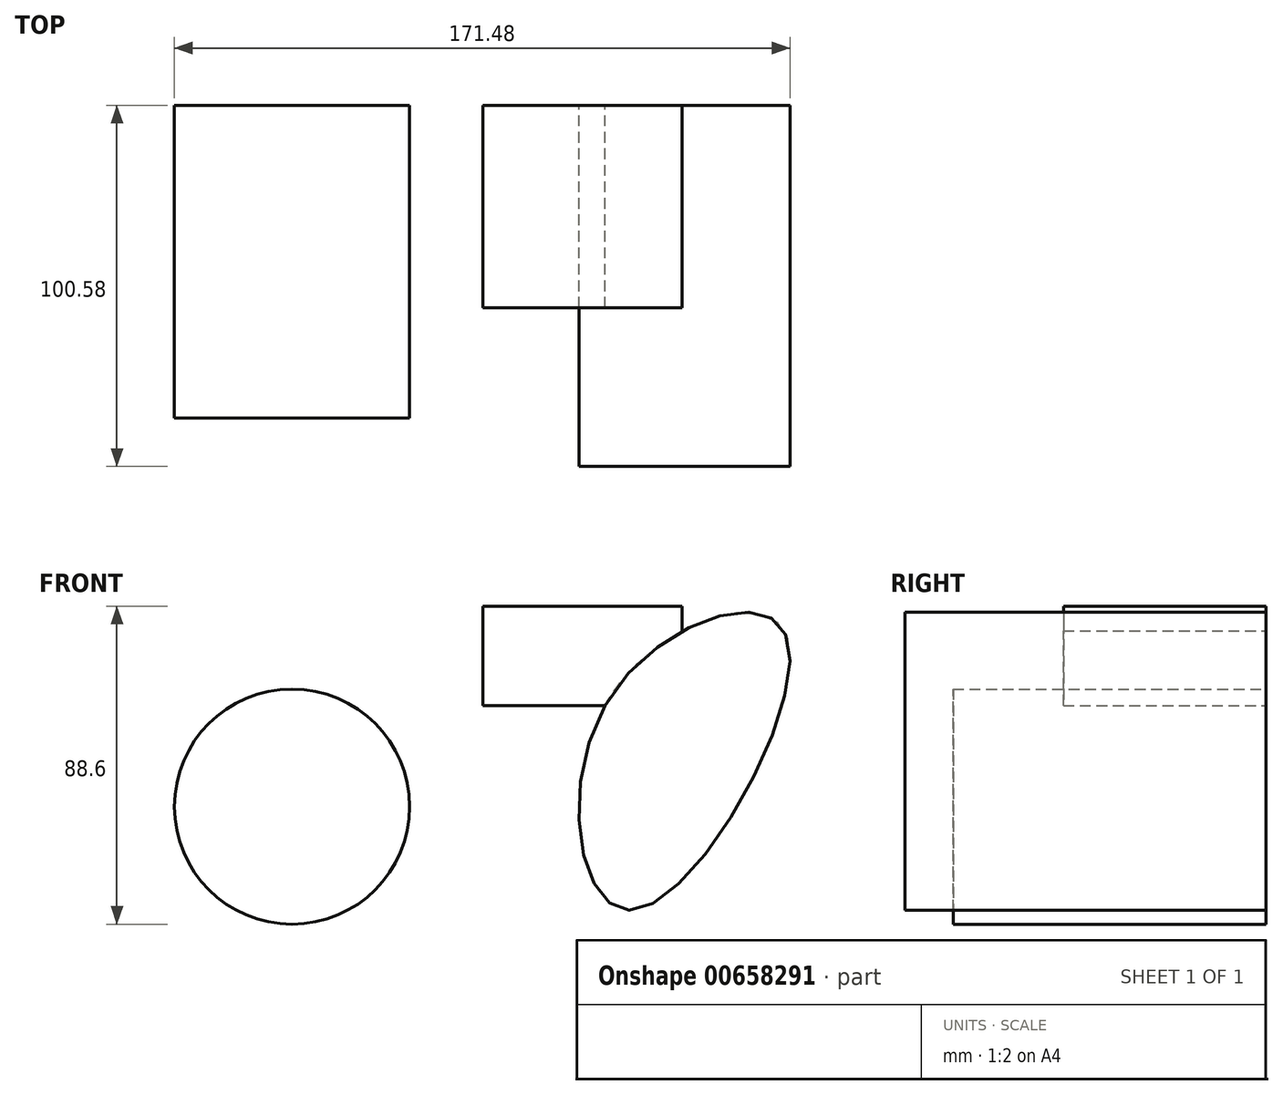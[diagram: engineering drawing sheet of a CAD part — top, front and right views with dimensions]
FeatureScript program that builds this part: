
annotation { "Feature Type Name" : "Feature", "Feature Type Description" : "" }
export const myFeature = defineFeature(function(context is Context, id is Id, definition is map)
    precondition{}
    {
        {
            var Q0;
            Q0=qCreatedBy(makeId("Front.planeOp"),FACE);
            var sketch = newSketch(context, id + "F0", { "sketchPlane" : qUnion([Q0])});
            skLineSegment(sketch, "E0.bottom", {"start": v(-113.94, 27.68) * mm, "end": v(-58.47, 27.68) * mm});
            skLineSegment(sketch, "E0.top", {"start": v(-113.94, 0) * mm, "end": v(-58.47, 0) * mm});
            skLineSegment(sketch, "E0.left", {"start": v(-113.94, 27.68) * mm, "end": v(-113.94, 0) * mm});
            skLineSegment(sketch, "E0.right", {"start": v(-58.47, 27.68) * mm, "end": v(-58.47, 0) * mm});
            skSolve(sketch);
        }
        {
            var Q0;
            Q0=makeQuery(id+"F0.imprint","IMPRINT",FACE,{"disambiguationData":[TD([[makeQuery(id+"F0.imprint","IMPRINT",EDGE,{"derivedFrom":sQuery(id+"F0.wireOp",EDGE,"E0.bottom")}),-1.0]])]});
            extrude(context, id + "F1", {"entities" : qUnion([Q0]), "depth" : 56.4 * mm, "offsetDistance" : 25.4 * mm});
        }
        {
            var Q0;
            Q0=qCreatedBy(makeId("Front.planeOp"),FACE);
            var sketch = newSketch(context, id + "F2", { "sketchPlane" : qUnion([Q0])});
            skFitSpline(sketch, "E1", {"points": [v(-79.93, 0) * mm, v(-29.7, 20.08) * mm, v(-72.08, -57.04) * mm, v(-79.93, 0) * mm]});
            skSolve(sketch);
        }
        {
            var Q0;
            Q0=makeQuery(id+"F2.imprint","IMPRINT",FACE,{"disambiguationData":[TD([[makeQuery(id+"F2.imprint","IMPRINT",EDGE,{"derivedFrom":sQuery(id+"F2.wireOp",EDGE,"E1")}),-1.0]])]});
            extrude(context, id + "F3", {"entities" : qUnion([Q0]), "operationType" : NewBodyOperationType.ADD, "depth" : 100.58 * mm, "offsetDistance" : 25.4 * mm});
        }
        {
            var Q0;
            Q0=qCreatedBy(makeId("Front.planeOp"),FACE);
            var sketch = newSketch(context, id + "F4", { "sketchPlane" : qUnion([Q0])});
            skCircle(sketch, "E2", {"center": v(-167.1, -28.16) * mm, "radius": 32.77 * mm});
            skSolve(sketch);
        }
        {
            var Q0;
            Q0=makeQuery(id+"F4.imprint","IMPRINT",FACE,{"disambiguationData":[TD([[makeQuery(id+"F4.imprint","IMPRINT",EDGE,{"derivedFrom":sQuery(id+"F4.wireOp",EDGE,"E2")}),1.0]])]});
            extrude(context, id + "F5", {"entities" : qUnion([Q0]), "depth" : 87.12 * mm, "offsetDistance" : 25.4 * mm});
        }
        {
            var Q0;
            Q0=qCreatedBy(makeId("Right.planeOp"),FACE);
            var sketch = newSketch(context, id + "F6", { "sketchPlane" : qUnion([Q0])});
            skArc(sketch, "E3", {"start": v(-174.44, 59.45) * mm, "mid": v(-140.03, -90.1) * mm, "end": v(-61.5, 41.73) * mm});
            skSolve(sketch);
        }
        {
            var Q0;
            Q0=sQuery(id+"F6.wireOp",EDGE,"E3");
            extrude(context, id + "F7", {"bodyType" : ToolBodyType.SURFACE, "surfaceEntities" : qUnion([Q0]), "depth" : 75.18 * mm, "offsetDistance" : 25.4 * mm});
        }
    });
